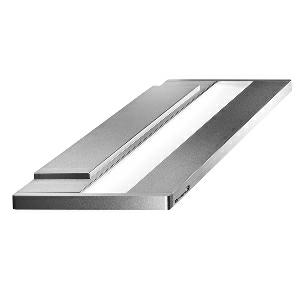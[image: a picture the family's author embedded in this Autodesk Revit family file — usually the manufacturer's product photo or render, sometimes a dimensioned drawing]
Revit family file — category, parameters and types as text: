
# Revit family: zera_bed_-_zew_9000_830_d_-_ul_dali_00812997_af94
name_source: partatom
category: Lighting Fixtures
units: mm (PartAtom-declared; Revit-internal decimal feet)

## family parameters
Cut with Voids When Loaded = No
Host = Face
Light Source = No
Part Type = Normal
Room Calculation Point = No
Round Connector Dimension = Use Diameter
Shared = No

## types (1)
- AL+UL (1 x LED, 7600 lm, 4000K/3000K)
    Apparent Load = 76 VA
    Approval mark = CE
    CIE Flux Codes = 45 81 99 31 100
    Color Rendering = 90/80
    Color Temperature = 4000K/3000K
    Default Elevation = 2000 mm  [stored 6.56168 ft]
    Description = ZEW 9000/830/D|Wall-mounted luminaire|light source:   Warm white   |work equipment: Power supply unit|luminous flux: 8500 lm|light distribution: Direct/indirect|class of protection: I|technology: Switchable|mains lead: Connector 5 pin|glare control: Diffusor|special features: General light, indirect, 3000K, Ra80, DALI Load 3x, DIN EN 60598-2-25, Reading light, direct, 2700K, Ra90, dir 4K 36W Ra95|
    Frequency = 50 Hz, 60 Hz
    Height = 20 mm  [stored 0.0656168 ft]
    Lamp = 1 x LED
    Lamp Light Flux = 7600 lm
    Lamp count = 1
    Length = 1050 mm
    Luminous efficacy = 100 lm/W
    Manufacturer = Waldmann
    ModVariant = No
    Model = 00812997
    Mounting Place = Wall
    Mounting Type = Surface mounted
    Number of Poles = 1
    OnlyDefault = Yes
    Power Factor = 1
    Product Name = ZERA.bed - ZEW 9000/830/D - UL/DALI
    Product group = Wall mounted Luminaire
    ProductGroupID = 20
    Protection Class = Protection class I
    Protection Degree = IP 20
    RLX_Detail_Level = 1
    RLX_Emergency_Light_Flux = 0 lm
    RLX_Emergency_Type = 0
    RLX_Emergency_Type_DB = No
    RlxData = <blob elided: 62681 chars, md5=e3d1e086>
    Socket = socket
    Standby Power = 0 W
    System Light Flux = 7600 lm
    System Power = 76 W
    Type Comments = General and Examation Light
    Type Image = zera_bed.jpg
    URL = http://relux.com
    VarID = al_ul_37f9
    Voltage = 230 V
    Voltage Range = 220-240 V
    Weight = 0.00 kg
    Width = 230 mm

note: [stored X ft] marks values corroborated as IEEE doubles in the binary element streams (Revit-internal decimal feet)

## geometry (parser evidence)
native form markers: Blend x4, Sweep x10
no freeform markers — native parametric forms only
